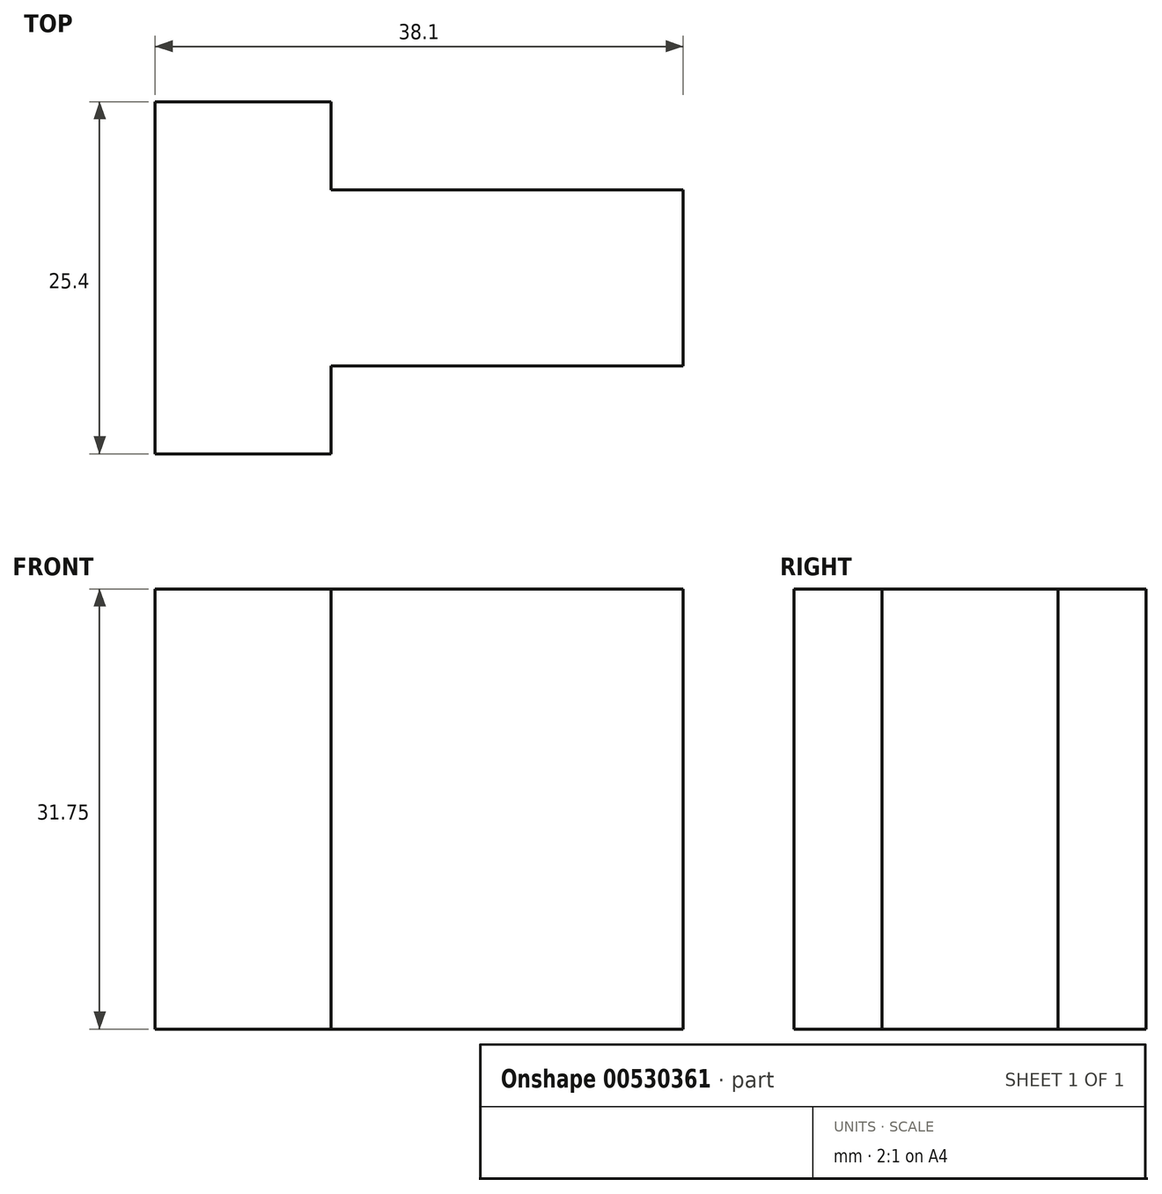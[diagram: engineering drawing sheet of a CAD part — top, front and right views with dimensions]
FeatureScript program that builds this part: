
annotation { "Feature Type Name" : "Feature", "Feature Type Description" : "" }
export const myFeature = defineFeature(function(context is Context, id is Id, definition is map)
    precondition{}
    {
        {
            var Q0;
            Q0=qCreatedBy(makeId("Top.planeOp"),FACE);
            var sketch = newSketch(context, id + "F0", { "sketchPlane" : qUnion([Q0])});
            skLineSegment(sketch, "E0", {"start": v(-57.5, 25.4) * mm, "end": v(-57.5, 0) * mm});
            skLineSegment(sketch, "E1", {"start": v(-57.5, 0) * mm, "end": v(-44.8, 0) * mm});
            skLineSegment(sketch, "E2", {"start": v(-44.8, 0) * mm, "end": v(-44.8, 6.35) * mm});
            skLineSegment(sketch, "E3", {"start": v(-44.8, 6.35) * mm, "end": v(-19.4, 6.35) * mm});
            skLineSegment(sketch, "E4", {"start": v(-19.4, 6.35) * mm, "end": v(-19.4, 19.05) * mm});
            skLineSegment(sketch, "E5", {"start": v(-19.4, 19.05) * mm, "end": v(-44.8, 19.05) * mm});
            skLineSegment(sketch, "E6", {"start": v(-44.8, 19.05) * mm, "end": v(-44.8, 25.4) * mm});
            skLineSegment(sketch, "E7", {"start": v(-44.8, 25.4) * mm, "end": v(-57.5, 25.4) * mm});
            skSolve(sketch);
        }
        {
            var Q0;
            Q0=makeQuery(id+"F0.imprint","IMPRINT",FACE,{"disambiguationData":[TD([[makeQuery(id+"F0.imprint","IMPRINT",EDGE,{"derivedFrom":sQuery(id+"F0.wireOp",EDGE,"E0")}),1.0]])]});
            extrude(context, id + "F1", {"entities" : qUnion([Q0]), "depth" : 31.75 * mm, "offsetDistance" : 25.4 * mm});
        }
    });
